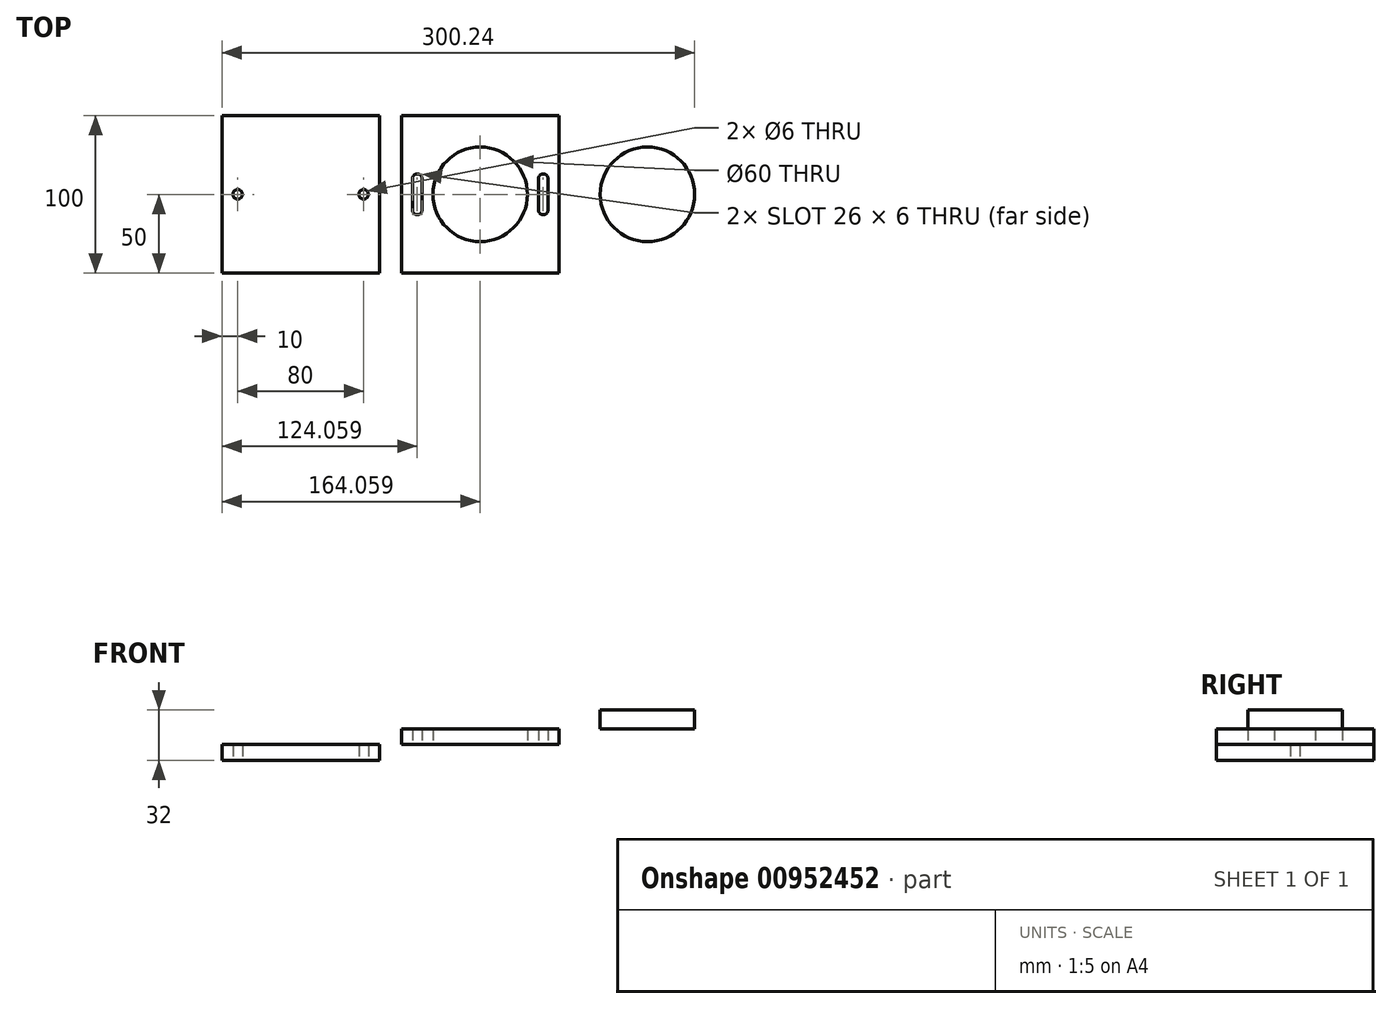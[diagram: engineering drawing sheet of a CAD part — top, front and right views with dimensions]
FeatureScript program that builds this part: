
annotation { "Feature Type Name" : "Feature", "Feature Type Description" : "" }
export const myFeature = defineFeature(function(context is Context, id is Id, definition is map)
    precondition{}
    {
        {
            var Q0;
            Q0=qCreatedBy(makeId("Top.planeOp"),FACE);
            var sketch = newSketch(context, id + "F0", { "sketchPlane" : qUnion([Q0])});
            skLineSegment(sketch, "E0.bottom", {"start": v(-50, 50) * mm, "end": v(50, 50) * mm});
            skLineSegment(sketch, "E0.top", {"start": v(-50, -50) * mm, "end": v(50, -50) * mm});
            skLineSegment(sketch, "E0.left", {"start": v(-50, 50) * mm, "end": v(-50, -50) * mm});
            skLineSegment(sketch, "E0.right", {"start": v(50, 50) * mm, "end": v(50, -50) * mm});
            skPoint(sketch, "E0.middle", {"position": v(0, 0) * mm});
            skCircle(sketch, "E1", {"center": v(-40, 0) * mm, "radius": 3 * mm});
            skCircle(sketch, "E2.MirrorC", {"center": v(40, 0) * mm, "radius": 3 * mm});
            skSolve(sketch);
        }
        {
            var Q0;
            Q0 = qSketchRegion(id + "F0", true);
            extrude(context, id + "F1", {"entities" : qUnion([Q0]), "depth" : 10 * mm, "offsetDistance" : 25 * mm});
        }
        {
            var Q0;
            Q0=makeQuery(id+"F1.opExtrude","CAP_FACE",FACE,{"disambiguationData":[OSD([sQuery(id+"F0.wireOp",EDGE,"E0.bottom"),sQuery(id+"F0.wireOp",EDGE,"E0.top"),sQuery(id+"F0.wireOp",EDGE,"E0.left"),sQuery(id+"F0.wireOp",EDGE,"E0.right"),sQuery(id+"F0.wireOp",EDGE,"E1"),sQuery(id+"F0.wireOp",EDGE,"E2.MirrorC")])],"isStart":false});
            var sketch = newSketch(context, id + "F2", { "sketchPlane" : qUnion([Q0])});
            skLineSegment(sketch, "E3.bottom", {"start": v(64.06, 50) * mm, "end": v(164.06, 50) * mm});
            skLineSegment(sketch, "E3.top", {"start": v(64.06, -50) * mm, "end": v(164.06, -50) * mm});
            skLineSegment(sketch, "E3.left", {"start": v(64.06, 50) * mm, "end": v(64.06, -50) * mm});
            skLineSegment(sketch, "E3.right", {"start": v(164.06, 50) * mm, "end": v(164.06, -50) * mm});
            skPoint(sketch, "E3.middle", {"position": v(114.06, 0) * mm});
            skCircle(sketch, "E4", {"center": v(114.06, 0) * mm, "radius": 30 * mm});
            skLineSegment(sketch, "E5.left", {"start": v(71.06, 10) * mm, "end": v(71.06, -10) * mm});
            skLineSegment(sketch, "E5.right", {"start": v(77.06, 10) * mm, "end": v(77.06, -10) * mm});
            skPoint(sketch, "E5.middle", {"position": v(74.06, 0) * mm});
            skArc(sketch, "E6", {"start": v(77.06, 10) * mm, "mid": v(74.06, 13) * mm, "end": v(71.06, 10) * mm});
            skArc(sketch, "E7", {"start": v(71.06, -10) * mm, "mid": v(74.06, -13) * mm, "end": v(77.06, -10) * mm});
            skLineSegment(sketch, "E8.MirrorCS", {"start": v(151.06, 10) * mm, "end": v(151.06, -10) * mm});
            skPoint(sketch, "E9.MirrorP", {"position": v(154.06, 0) * mm});
            skArc(sketch, "E10.MirrorCS", {"start": v(157.06, -10) * mm, "mid": v(154.06, -13) * mm, "end": v(151.06, -10) * mm});
            skArc(sketch, "E11.MirrorCS", {"start": v(151.06, 10) * mm, "mid": v(154.06, 13) * mm, "end": v(157.06, 10) * mm});
            skLineSegment(sketch, "E12.MirrorCS", {"start": v(157.06, 10) * mm, "end": v(157.06, -10) * mm});
            skSolve(sketch);
        }
        {
            var Q0;
            Q0 = qSketchRegion(id + "F2", true);
            extrude(context, id + "F3", {"entities" : qUnion([Q0]), "depth" : 10 * mm, "offsetDistance" : 25 * mm});
        }
        {
            var Q0;
            Q0=makeQuery(id+"F3.opExtrude","CAP_FACE",FACE,{"disambiguationData":[OSD([sQuery(id+"F2.wireOp",EDGE,"E3.bottom"),sQuery(id+"F2.wireOp",EDGE,"E3.top"),sQuery(id+"F2.wireOp",EDGE,"E3.left"),sQuery(id+"F2.wireOp",EDGE,"E3.right"),sQuery(id+"F2.wireOp",EDGE,"E4"),sQuery(id+"F2.wireOp",EDGE,"E5.left"),sQuery(id+"F2.wireOp",EDGE,"E5.right"),sQuery(id+"F2.wireOp",EDGE,"E6"),sQuery(id+"F2.wireOp",EDGE,"E7"),sQuery(id+"F2.wireOp",EDGE,"E8.MirrorCS"),sQuery(id+"F2.wireOp",EDGE,"E10.MirrorCS"),sQuery(id+"F2.wireOp",EDGE,"E11.MirrorCS"),sQuery(id+"F2.wireOp",EDGE,"E12.MirrorCS")])],"isStart":false});
            var sketch = newSketch(context, id + "F4", { "sketchPlane" : qUnion([Q0])});
            skCircle(sketch, "E13", {"center": v(220.24, 0) * mm, "radius": 30 * mm});
            skSolve(sketch);
        }
        {
            var Q0;
            Q0 = qSketchRegion(id + "F4", true);
            extrude(context, id + "F5", {"entities" : qUnion([Q0]), "depth" : 12 * mm, "offsetDistance" : 25 * mm});
        }
    });
